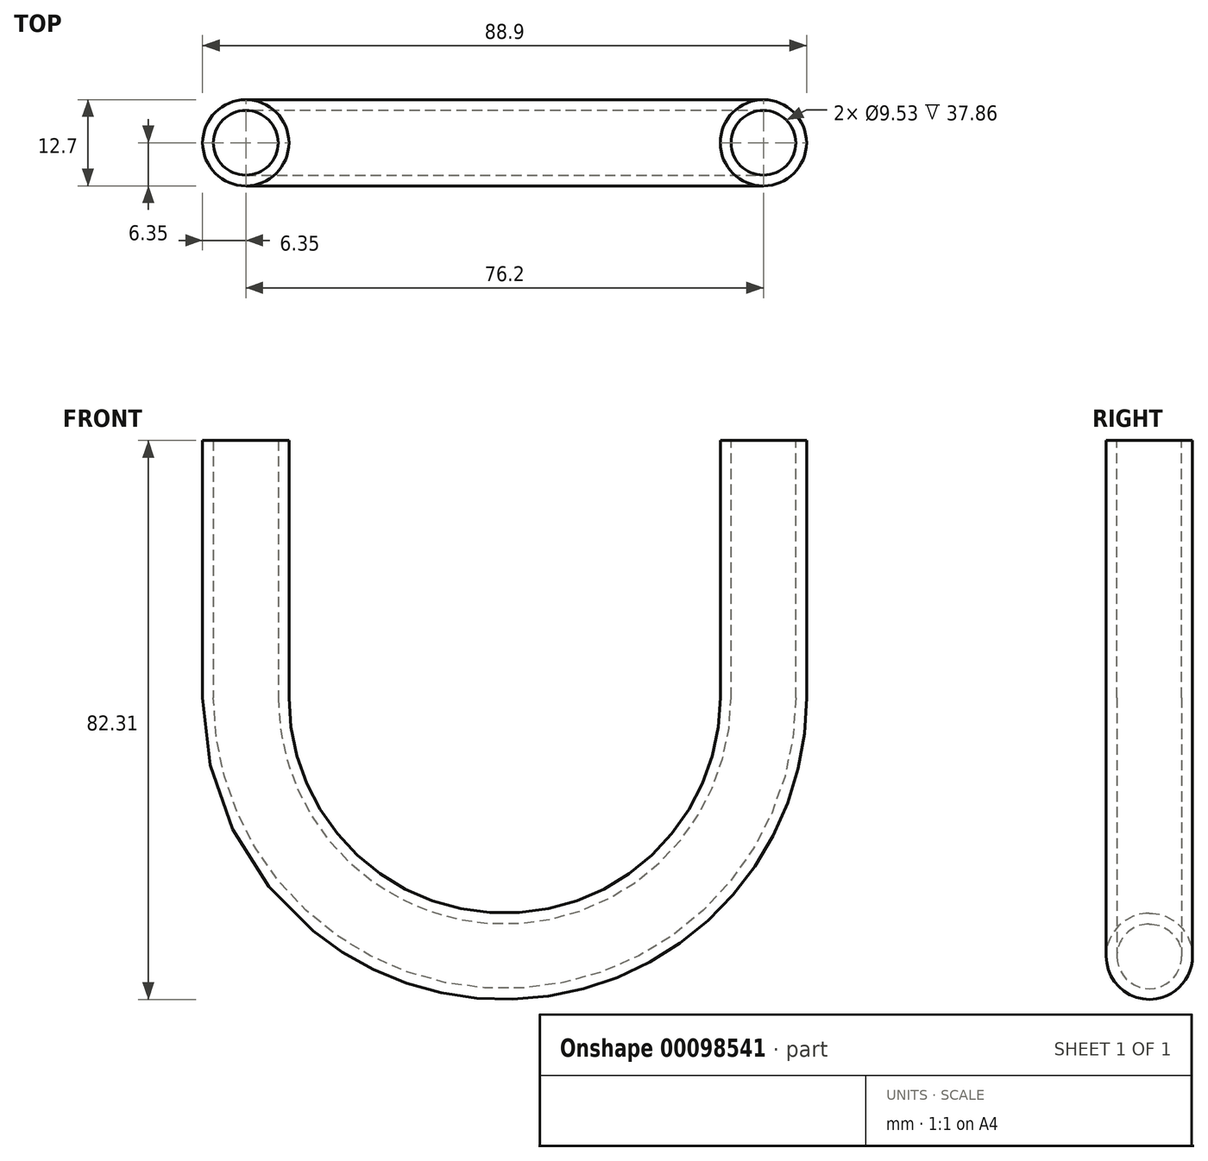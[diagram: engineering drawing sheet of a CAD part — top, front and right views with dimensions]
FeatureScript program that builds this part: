
annotation { "Feature Type Name" : "Feature", "Feature Type Description" : "" }
export const myFeature = defineFeature(function(context is Context, id is Id, definition is map)
    precondition{}
    {
        {
            var Q0;
            Q0=qCreatedBy(makeId("Top.planeOp"),FACE);
            var sketch = newSketch(context, id + "F0", { "sketchPlane" : qUnion([Q0])});
            skCircle(sketch, "E0", {"center": v(0, 0) * mm, "radius": 6.35 * mm});
            skCircle(sketch, "E1", {"center": v(0, 0) * mm, "radius": 4.76 * mm});
            skSolve(sketch);
        }
        {
            var Q0;
            Q0=qCreatedBy(makeId("Front.planeOp"),FACE);
            var sketch = newSketch(context, id + "F1", { "sketchPlane" : qUnion([Q0])});
            skLineSegment(sketch, "E2", {"start": v(0, 0) * mm, "end": v(0, -37.86) * mm});
            skLineSegment(sketch, "E3", {"start": v(76.2, 0) * mm, "end": v(76.2, -37.86) * mm});
            skArc(sketch, "E4", {"start": v(0, -37.86) * mm, "mid": v(38.1, -75.96) * mm, "end": v(76.2, -37.86) * mm});
            skSolve(sketch);
        }
        {
            var Q0;
            Q0=makeQuery(id+"F0.imprint","IMPRINT",FACE,{"disambiguationData":[TD([[makeQuery(id+"F0.imprint","IMPRINT",EDGE,{"derivedFrom":sQuery(id+"F0.wireOp",EDGE,"E0")}),1.0]])]});
            var Q1;
            Q1=sQuery(id+"F1.wireOp",EDGE,"E2");
            var Q2;
            Q2=sQuery(id+"F1.wireOp",EDGE,"E4");
            var Q3;
            Q3=sQuery(id+"F1.wireOp",EDGE,"E3");
            sweep(context, id + "F2", {"profiles" : qUnion([Q0]), "path" : qUnion([Q1, Q2, Q3])});
        }
    });
